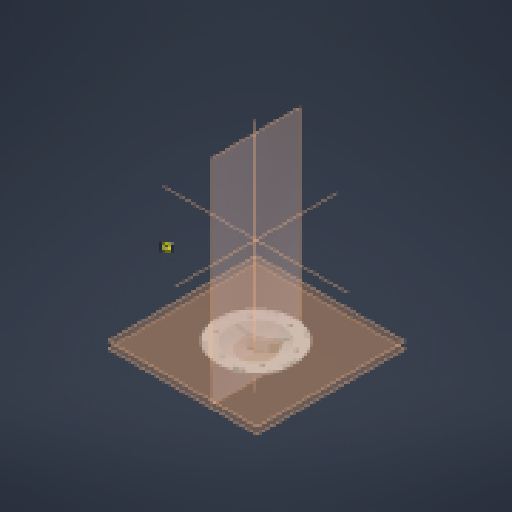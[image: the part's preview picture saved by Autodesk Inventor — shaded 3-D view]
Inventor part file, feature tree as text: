
AUTODESK INVENTOR PART (.ipt)
format: ipt  version: 2023 (Build 270158000, 158)  size: 3,820,544 bytes
history: native  units: mm
features: sketch x16, extrude x10, other x8, projected_geometry x7, plane x5, pattern_circular x4, reference x3, revolve x2, chamfer x2, sweep x1, shell x1
ambient origin geometry x8: Origin, YZ Plane, XZ Plane, XY Plane, X Axis, Y Axis, Z Axis, Center Point
bodies: Solid1 (feature_tree)
feature tree (59):
  revolve  "Revolution1"  [1 undecoded]
  sketch  "3D Sketch1"
  plane  "Work Plane1"
  sweep  "Sweep1"
  pattern_circular  "Circular Pattern1"  Count=6 Angle=360.0deg
  extrude  "Extrusion1"  TaperAngle=0.0deg  [1 undecoded]
  plane  "Work Plane3"
  sketch  "Sketch12"  dims[d16=0.2mm]
  plane  "Work Plane6"
  extrude  "Extrusion6"  Depth=10.0mm
  chamfer  "Chamfer2"  Distance=10.0mm
  pattern_circular  "Circular Pattern4"  [2 undecoded]
  shell  "Shell2"  Thickness=30.0mm
  extrude  "Extrusion8"  Depth=100.0mm
  extrude  "Extrusion2"  Depth=6.0mm
  sketch  "Sketch7"  dims[d13=1.6mm]
  plane  "Work Plane4"
  extrude  "Extrusion3"  Depth=4.0mm TaperAngle=0.0deg
  extrude  "Extrusion4"  Depth=3.5mm TaperAngle=45.0deg
  pattern_circular  "Circular Pattern2"  Count=3 Angle=360.0deg
  extrude  "Extrusion7"  TaperAngle=30.0deg  [1 undecoded]
  pattern_circular  "Circular Pattern5"  [2 undecoded]
  revolve  "Revolution2"  [1 undecoded]
  extrude  "Extrusion9"  Depth=60.0mm TaperAngle=360.0deg
  extrude  "Extrusion12"  TaperAngle=360.0deg  [1 undecoded]
  extrude  "Extrusion13"  Depth=130.0mm
  chamfer  "Chamfer3"  [1 undecoded]
  sketch  "Sketch1"  dims[d0=160.0mm d1=100.0mm]
  other  "Helical Curve2"
  other  "Project to Surface1"
  sketch  "Sketch2"  dims[d2=90.0deg d7=1200.0mm d8=637.649mm d9=252.623mm d10=0.0mm]
  sketch  "Sketch3"  dims[d11=15.0mm]
  plane  "Work Plane2"
  sketch  "Sketch6"  dims[d12=3.0mm]
  sketch  "Sketch8"  dims[d14=1.478932mm]
  sketch  "Sketch9"  dims[d15=0.2mm]
  sketch  "Sketch13"  dims[d17=0.2mm]
  sketch  "Sketch14"  dims[d18=0.0mm d19=0.0mm d20=60.0mm d21=360.0deg]
  reference  "Reference1"
  sketch  "Sketch15"  dims[d23=120.0mm d24=0.0mm d25=0.0mm]
  sketch  "Sketch16"  dims[d26=-130.0mm d27=-10.0mm d29=1.0mm d30=10.0mm d31=0.0mm]
  sketch  "Sketch17"  dims[d32=6.0mm]
  sketch  "Sketch21"  dims[d33=4.0mm d34=0.0mm]
  reference  "Reference5"
  reference  "Reference6"
  sketch  "Sketch22"  dims[d35=4.0mm d36=4.0mm d37=0.0mm d38=30.0mm d39=360.0deg d51=100.0mm d52=6.0mm d53=4.0mm d54=0.0mm d55=3.5mm d56=1.0mm d57=45.0deg d58=30.0mm d59=360.0deg d61=30.0deg d62=6.0mm d63=4.0mm d64=0.0mm d65=60.0mm d66=360.0deg d68=360.0deg d69=130.0mm d70=0.0mm d71=0.0mm d72=130.0mm d73=0.0mm d74=0.0mm d80=12.2mm d81=0.0mm d82=12.0mm d83=0.0mm d84=0.0mm d85=5.0mm d86=2.0mm d87=45.0deg d88=37.0mm]
  projected_geometry  "Projected Loop1"
  projected_geometry  "Project Cut Edges1"
  projected_geometry  "Project Cut Edges2"
  projected_geometry  "Project Cut Edges3"
  projected_geometry  "Project Cut Edges5"
  projected_geometry  "Project Cut Edges6"
  parser-record x2  (decoder bookkeeping rows leaked as tree rows — omitted from the tree; the rows remain in map.json)
  other  "Assembly1.iam"
  other  "lower_centering_ring:1"
  projected_geometry  "Project Cut Edges7"
  other  "assembly.iam"
  other  "deckel:1"
note: 10 required parameter values undecoded (feature->parameter linkage not recoverable at this tier; creation-order binding heuristic only, values carry confidence <= 0.55)
note: 2 file-system paths scrubbed to <path> (originals preserved in map.json)